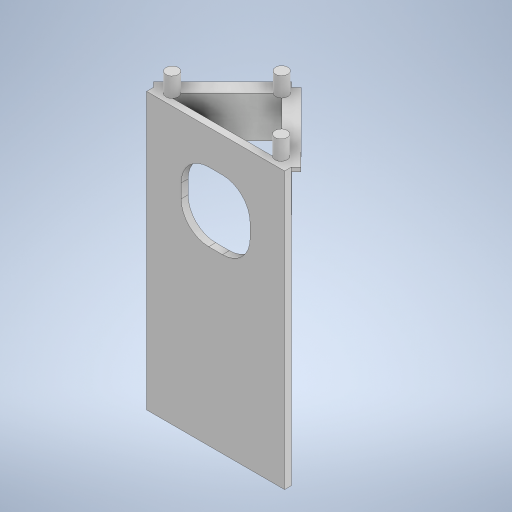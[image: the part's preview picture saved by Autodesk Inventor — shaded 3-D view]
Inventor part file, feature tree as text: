
AUTODESK INVENTOR PART (.ipt)
format: ipt  version: 2023 (Build 270158000, 158)  size: 315,392 bytes
history: native  units: mm
features: extrude x5, sketch x5
ambient origin geometry x8: Origin, YZ Plane, XZ Plane, XY Plane, X Axis, Y Axis, Z Axis, Center Point
bodies: Solid1 (feature_tree)
feature tree (10):
  extrude  "Extrusion1"  Depth=200.0mm
  extrude  "Extrusion2"  TaperAngle=45.0deg  [1 undecoded]
  extrude  "Extrusion6"  Depth=5.0mm
  extrude  "Extrusion9"  Depth=50.0mm
  extrude  "Extrusion10"  Depth=20.0mm
  sketch  "Sketch1"  dims[d0=100.0mm d1=200.0mm]
  sketch  "Sketch2"  dims[d2=5.0mm d3=0.0mm d4=45.0deg]
  sketch  "Sketch6"  dims[d5=5.0mm d6=5.0mm]
  sketch  "Sketch10"  dims[d7=30.0mm d8=0.0mm d21=50.0mm]
  sketch  "Sketch12"  dims[d22=50.0mm d23=20.0mm d24=5.0mm d25=0.0mm d33=5.0mm d34=5.0mm d36=3.0mm d37=0.0mm d38=9.0mm d39=9.0mm d41=9.0mm d42=14.0mm d43=0.0mm]
note: 1 required parameter value undecoded (feature->parameter linkage not recoverable at this tier; creation-order binding heuristic only, values carry confidence <= 0.55)
